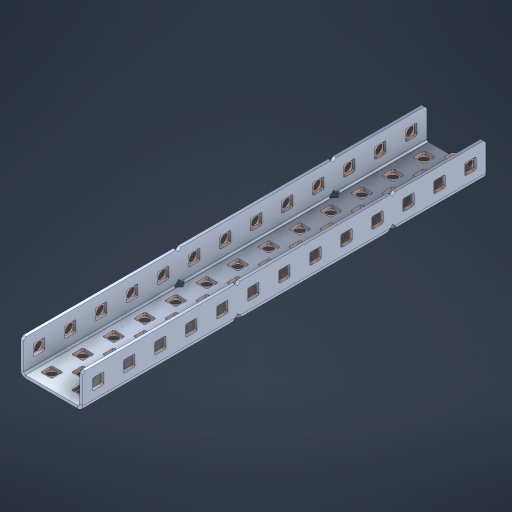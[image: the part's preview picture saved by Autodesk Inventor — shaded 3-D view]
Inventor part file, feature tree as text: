
AUTODESK INVENTOR PART (.ipt)
format: ipt  version: 2023 (Build 270158000, 158)  size: 1,072,128 bytes
history: native  units: in
note: dims shown in document units (in); Inventor stores cm internally (conversion verified against a paired STEP export)
features: other x72, extrude x63, sheet_metal_op x11, sketch x10, pattern_linear x2, mirror x1, chamfer x1
ambient origin geometry x8: Origin, YZ Plane, XZ Plane, XY Plane, X Axis, Y Axis, Z Axis, Center Point
bodies: Solid1 (feature_tree), Body (feature_tree)
feature tree (160):
  sheet_metal_op  "Flanges"
  other  "Flange Pattern Plane"
  other  "Flange Pattern Sketch"
  sheet_metal_op  "Flange Pattern"
  sheet_metal_op  "Body Pattern"
  pattern_linear  "Center Pattern"  Spacing1=0.0469in  [1 undecoded]
  other  "Arc Length"
  mirror  "Notch Mirror"
  pattern_linear  "Notch Pattern"  Spacing1=0.182in  [1 undecoded]
  chamfer  "End Chamfer"
  extrude  "Half Cut"  Depth=0.02in
  sketch  "Sketch1"  dims[d0=1.0in]
  other  "Plate1"
  sketch  "Sketch2"  dims[d1=6.5in]
  other  "Plate2"
  sheet_metal_op  "Bend1"
  sheet_metal_op  "Corner1"
  sketch  "Sketch3"  dims[d2=0.0469in]
  sketch  "Sketch7"  dims[d3=0.0469in]
  other  "Srf1"
  other  "Srf2"
  sketch  "Sketch8"  dims[d4=0.0234in]
  sketch  "Sketch9"  dims[d5=0.0938in]
  other  "Srf91"
  sheet_metal_op  "Body Pattern Sketch"
  other  "Srf92"
  sketch  "Sketch13"  dims[d6=0.0469in]
  sketch  "Sketch14"  dims[d7=0.5in d8=90.0deg d9=0.0312in]
  sketch  "Sketch15"  dims[d10=0.1875in]
  sketch  "Sketch16"  dims[d11=0.0469in d12=0.0469in d16=0.182in d17=0.02in d18=0.0469in d19=0.0in d20=0.25in d21=0.25in d38=5.1181in d40=0.5in d41=0.7874in d43=1.0in d46=0.172in d47=1.0in d48=0.0in d49=0.182in d50=0.02in d51=0.25in d52=0.25in d53=0.0469in d54=0.0in d55=0.172in d56=1.0in d57=0.0in d58=0.25in d60=5.1181in d62=0.5in d63=0.7874in d65=0.5in d85=0.1227in d86=0.1659in d88=0.04in d89=0.0469in d90=0.0in d91=0.04in d92=0.0491in d95=2.5in d96=0.04in d97=0.25in d98=45.0deg d99=0.25in d100=0.5in d101=0.0in d102=2.497in d106=0.182in d107=0.02in d108=0.5in d109=0.5in d110=0.0469in d111=0.0in d112=0.172in d113=0.5in d114=0.0in d117=0.5in d118=0.5in d119=0.5in]
  other  "Srf786"
  other  "Srf823"
  other  "Srf824"
  other  "Srf825"
  other  "Srf826"
  other  "Srf827"
  other  "Srf828"
  other  "Srf829"
  other  "Srf856"
  other  "Srf857"
  other  "Srf858"
  other  "Srf859"
  other  "Srf860"
  other  "Srf861"
  other  "Srf862"
  other  "Srf889"
  other  "Srf890"
  other  "Srf891"
  other  "Srf892"
  other  "Srf893"
  other  "Srf894"
  other  "Srf895"
  other  "Srf896"
  other  "Srf922"
  other  "Srf923"
  other  "Srf924"
  other  "Srf925"
  other  "Srf926"
  other  "Srf959"
  other  "Srf960"
  other  "Srf961"
  other  "Srf962"
  other  "Srf963"
  other  "Srf996"
  other  "Srf997"
  other  "Srf998"
  other  "Srf999"
  other  "Srf1143"
  other  "Srf1144"
  other  "Srf1145"
  other  "Srf1146"
  other  "Srf1147"
  other  "Srf1148"
  other  "Srf1149"
  other  "Srf1150"
  other  "Srf1151"
  other  "Srf1152"
  other  "Srf1153"
  other  "Srf1154"
  other  "Srf1199"
  other  "Srf1200"
  other  "Srf1201"
  other  "Srf1202"
  other  "Srf1203"
  other  "Srf1204"
  other  "Srf1205"
  other  "Srf1206"
  other  "Srf1207"
  other  "Srf1208"
  other  "Srf1209"
  other  "Srf1210"
  sheet_metal_op  "Flange Stamp"
  sheet_metal_op  "Flange Circle"
  sheet_metal_op  "Body Stamp"
  sheet_metal_op  "Body Circle"
  other  "Center Stamp"
  other  "Center Circle"
  sheet_metal_op  "Notch"
  extrude  "ExtrusionSrf2"  Depth=0.0469in
  extrude  "ExtrusionSrf92"  TaperAngle=0.0deg  [1 undecoded]
  extrude  "ExtrusionSrf823"  Depth=0.5in
  extrude  "ExtrusionSrf824"  Depth=0.5in
  extrude  "ExtrusionSrf825"  Depth=0.5in
  extrude  "ExtrusionSrf826"  Depth=0.5in
  extrude  "ExtrusionSrf827"  Depth=1.0in TaperAngle=0.0deg
  extrude  "ExtrusionSrf828"  Depth=0.5in
  extrude  "ExtrusionSrf829"  Depth=0.02in
  extrude  "ExtrusionSrf856"  Depth=0.5in
  extrude  "ExtrusionSrf857"  Depth=0.5in
  extrude  "ExtrusionSrf858"  Depth=0.0469in
  extrude  "ExtrusionSrf859"  TaperAngle=0.0deg  [1 undecoded]
  extrude  "ExtrusionSrf860"  Depth=0.5in
  extrude  "ExtrusionSrf861"  Depth=1.0in TaperAngle=0.0deg
  extrude  "ExtrusionSrf862"  Depth=0.5in
  extrude  "ExtrusionSrf889"  Depth=0.5in
  extrude  "ExtrusionSrf890"  Depth=0.5in
  extrude  "ExtrusionSrf891"  Depth=0.5in
  extrude  "ExtrusionSrf892"  Depth=0.5in
  extrude  "ExtrusionSrf893"  Depth=0.5in
  extrude  "ExtrusionSrf894"  Depth=0.0469in
  extrude  "ExtrusionSrf895"  TaperAngle=0.0deg  [1 undecoded]
  extrude  "ExtrusionSrf896"  Depth=0.5in
  extrude  "ExtrusionSrf922"  Depth=0.5in
  extrude  "ExtrusionSrf923"  Depth=2.5in
  extrude  "ExtrusionSrf924"  Depth=0.5in TaperAngle=45.0deg
  extrude  "ExtrusionSrf925"  Depth=0.5in
  extrude  "ExtrusionSrf926"  Depth=0.5in TaperAngle=0.0deg
  extrude  "ExtrusionSrf959"  Depth=0.5in
  extrude  "ExtrusionSrf960"  Depth=0.5in
  extrude  "ExtrusionSrf961"  Depth=0.02in
  extrude  "ExtrusionSrf962"  Depth=0.5in
  extrude  "ExtrusionSrf963"  Depth=0.5in
  extrude  "ExtrusionSrf996"  Depth=0.0469in
  extrude  "ExtrusionSrf997"  TaperAngle=0.0deg  [1 undecoded]
  extrude  "ExtrusionSrf998"  Depth=0.5in
  extrude  "ExtrusionSrf999"  Depth=0.5in TaperAngle=0.0deg
  extrude  "ExtrusionSrf1143"  Depth=0.5in
  extrude  "ExtrusionSrf1144"  Depth=0.5in
  extrude  "ExtrusionSrf1145"  Depth=0.5in
  extrude  "ExtrusionSrf1146"  [1 undecoded]
  extrude  "ExtrusionSrf1147"  [1 undecoded]
  extrude  "ExtrusionSrf1148"  [1 undecoded]
  extrude  "ExtrusionSrf1149"  [1 undecoded]
  extrude  "ExtrusionSrf1150"  [1 undecoded]
  extrude  "ExtrusionSrf1151"  [1 undecoded]
  extrude  "ExtrusionSrf1152"  [1 undecoded]
  extrude  "ExtrusionSrf1153"  [1 undecoded]
  extrude  "ExtrusionSrf1154"  [1 undecoded]
  extrude  "ExtrusionSrf1199"  [1 undecoded]
  extrude  "ExtrusionSrf1200"  [1 undecoded]
  extrude  "ExtrusionSrf1201"  [1 undecoded]
  extrude  "ExtrusionSrf1202"  [1 undecoded]
  extrude  "ExtrusionSrf1203"  [1 undecoded]
  extrude  "ExtrusionSrf1204"  [1 undecoded]
  extrude  "ExtrusionSrf1205"  [1 undecoded]
  extrude  "ExtrusionSrf1206"  [1 undecoded]
  extrude  "ExtrusionSrf1207"  [1 undecoded]
  extrude  "ExtrusionSrf1208"  [1 undecoded]
  extrude  "ExtrusionSrf1209"  [1 undecoded]
  extrude  "ExtrusionSrf1210"  [1 undecoded]
note: 27 required parameter values undecoded (feature->parameter linkage not recoverable at this tier; creation-order binding heuristic only, values carry confidence <= 0.55)
